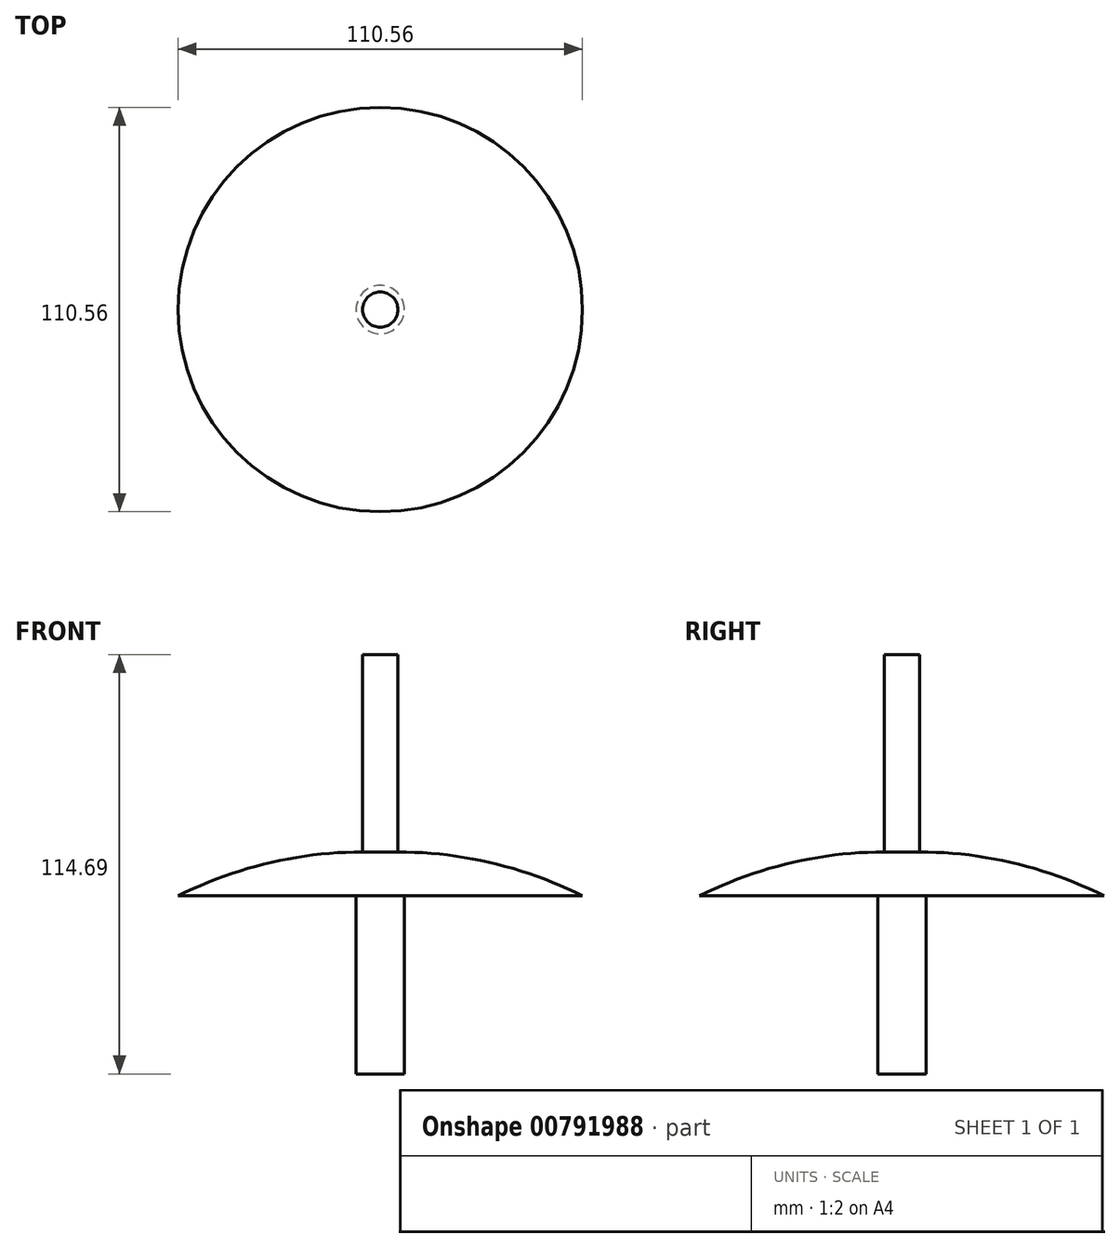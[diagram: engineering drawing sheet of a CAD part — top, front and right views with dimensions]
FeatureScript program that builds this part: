
annotation { "Feature Type Name" : "Feature", "Feature Type Description" : "" }
export const myFeature = defineFeature(function(context is Context, id is Id, definition is map)
    precondition{}
    {
        {
            var Q0;
            Q0=qCreatedBy(makeId("Front.planeOp"),FACE);
            var sketch = newSketch(context, id + "F0", { "sketchPlane" : qUnion([Q0])});
            skLineSegment(sketch, "E0", {"start": v(0, 61.19) * mm, "end": v(4.83, 61.19) * mm});
            skLineSegment(sketch, "E1", {"start": v(4.83, 61.19) * mm, "end": v(4.83, 7.2) * mm});
            skArc(sketch, "E2", {"start": v(55.28, -4.83) * mm, "mid": v(30.75, 4.12) * mm, "end": v(4.83, 7.2) * mm});
            skLineSegment(sketch, "E3", {"start": v(55.28, -4.83) * mm, "end": v(6.6, -4.83) * mm});
            skLineSegment(sketch, "E4", {"start": v(6.6, -4.83) * mm, "end": v(6.6, -53.5) * mm});
            skLineSegment(sketch, "E5", {"start": v(6.6, -53.5) * mm, "end": v(0, -53.5) * mm});
            skLineSegment(sketch, "E6", {"start": v(0, -53.5) * mm, "end": v(0, 61.19) * mm});
            skSolve(sketch);
        }
        {
            var Q0;
            Q0=makeQuery(id+"F0.imprint","IMPRINT",FACE,{"disambiguationData":[TD([[makeQuery(id+"F0.imprint","IMPRINT",EDGE,{"derivedFrom":sQuery(id+"F0.wireOp",EDGE,"E0")}),-1.0]])]});
            var Q1;
            Q1=sQuery(id+"F0.wireOp",EDGE,"E6");
            revolve(context, id + "F1", {"surfaceOperationType" : NewSurfaceOperationType.NEW, "entities" : qUnion([Q0]), "axis" : qUnion([Q1]), "revolveType" : RevolveType.FULL});
        }
    });
